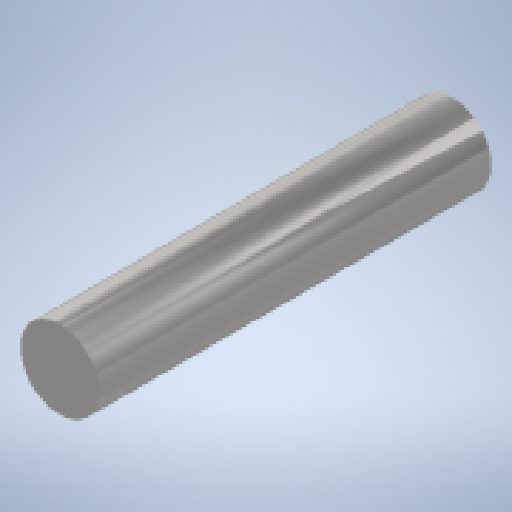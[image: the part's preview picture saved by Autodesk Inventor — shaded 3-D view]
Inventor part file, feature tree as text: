
AUTODESK INVENTOR PART (.ipt)
format: ipt  version: 2024 (Build 280153000, 153)  size: 136,704 bytes
history: native  units: mm
features: other x1, extrude x1, sketch x1
ambient origin geometry x8: Origin, YZ Plane, XZ Plane, XY Plane, X Axis, Y Axis, Z Axis, Center Point
bodies: Body1 (feature_tree)
feature tree (3):
  other  "ソリッド1"
  extrude  "押し出し1"  Depth=4.0mm
  sketch  "スケッチ1"
